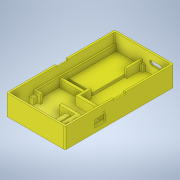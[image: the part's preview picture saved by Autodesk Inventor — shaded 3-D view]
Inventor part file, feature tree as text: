
AUTODESK INVENTOR PART (.ipt)
format: ipt  version: 2020.1 (Build 241239000, 239)  size: 795,136 bytes
history: native  units: mm
features: extrude x18, sketch x9, chamfer x4, plane x2, fillet x2, emboss x2
ambient origin geometry x8: Origin, YZ Plane, XZ Plane, XY Plane, X Axis, Y Axis, Z Axis, Center Point
bodies: Solid1 (feature_tree)
feature tree (37):
  sketch  "Sketch1"  dims[d4=1.2mm d6=1.2mm]
  extrude  "Extrusion1"  Depth=1.2mm
  extrude  "Extrusion2"  Depth=1.2mm TaperAngle=0.0deg
  plane  "Work Plane1"
  extrude  "Extrusion6"  Depth=3.2mm
  extrude  "Extrusion5"  Depth=6.25mm
  extrude  "Extrusion7"  Depth=16.8mm
  extrude  "Extrusion8"  Depth=1.2mm
  extrude  "Extrusion9"  Depth=38.0mm
  fillet  "Fillet1"  Radius=1.5mm
  chamfer  "Chamfer2"  Distance=1.5mm
  extrude  "Extrusion10"  Depth=4.0mm
  extrude  "Extrusion11"  Depth=3.0mm
  chamfer  "Chamfer1"  Distance=3.0mm
  plane  "Work Plane2"
  extrude  "Extrusion14"  Depth=3.0mm
  extrude  "Extrusion15"  Depth=3.5mm
  extrude  "Extrusion16"  Depth=2.4mm
  extrude  "Extrusion17"  Depth=10.0mm
  chamfer  "Chamfer4"  Distance=1.38mm
  chamfer  "Chamfer5"  Distance=1.28mm
  extrude  "Extrusion21"  Depth=1.0mm TaperAngle=0.0deg
  extrude  "Extrusion22"  Depth=25.0mm
  emboss  "Emboss2"
  extrude  "Extrusion23"  Depth=2.0mm TaperAngle=0.0deg
  fillet  "Fillet3"  Radius=2.2mm
  extrude  "Extrusion24"  Depth=5.1mm
  emboss  "Emboss3"
  extrude  "Extrusion25"  Depth=2.0mm TaperAngle=0.0deg
  sketch  "Sketch4"  dims[d7=1.0mm d8=1.2mm d9=0.0mm]
  sketch  "Sketch7"  dims[d10=13.0mm d11=0.0mm]
  sketch  "Sketch12"  dims[d20=18.1mm d21=43.6mm d22=29.1mm d23=15.35mm d28=1.2mm d29=3.2mm]
  sketch  "Sketch13"  dims[d33=6.25mm d35=3.85mm]
  sketch  "Sketch17"  dims[d37=8.0mm d38=16.8mm]
  sketch  "Sketch18"  dims[d39=55.5mm d42=1.2mm]
  sketch  "Sketch19"  dims[d46=1.2mm d47=0.0mm d48=38.0mm d49=1.5mm]
  sketch  "Sketch20"  dims[d50=1.2mm d51=1.5mm d52=4.0mm d60=3.0mm d61=3.0mm d62=3.0mm d73=3.5mm d74=2.4mm d75=1.4mm d76=1.38mm d77=1.28mm d81=1.0mm d82=0.0mm d83=25.0mm d84=2.0mm d85=0.0mm d86=2.2mm d87=0.0mm d88=5.1mm d89=2.0mm d90=0.0mm d91=2.0mm d92=0.0mm d93=0.5mm d94=0.3mm d95=0.0mm d96=2.0mm d97=0.0mm d98=1.0mm d99=2.0mm d100=45.0deg d103=0.5mm d104=2.0mm d105=45.0deg d109=7.9mm d110=3.0mm d111=0.0mm d113=8.0mm d114=1.0mm d115=3.0mm d116=0.0mm d118=3.0mm d119=0.0mm d120=13.5mm d121=3.1mm d122=3.0mm d123=3.0mm d124=0.0mm d135=0.5mm d136=2.0mm d137=45.0deg d145=0.1mm d146=2.0mm d147=45.0deg d154=2.0mm d155=2.0mm d156=2.0mm d157=2.0mm d162=33.5mm d163=2.0mm d164=0.0mm d166=2.0mm d167=5.0mm d168=0.0mm d169=38.0mm d170=0.2mm d171=0.0mm d172=3.0mm d173=3.0mm d191=0.2mm d192=2.2mm d193=1.0mm d194=1.0mm d195=2.0mm d196=0.0mm d197=1.1mm d198=3.0mm d199=8.0mm d200=22.5deg d201=45.0deg d202=1.6mm d203=10.0mm d204=0.0mm d205=7.62mm d206=2.54mm d207=0.5mm d208=0.0mm d209=1.3mm d210=10.0mm d211=0.0mm]
